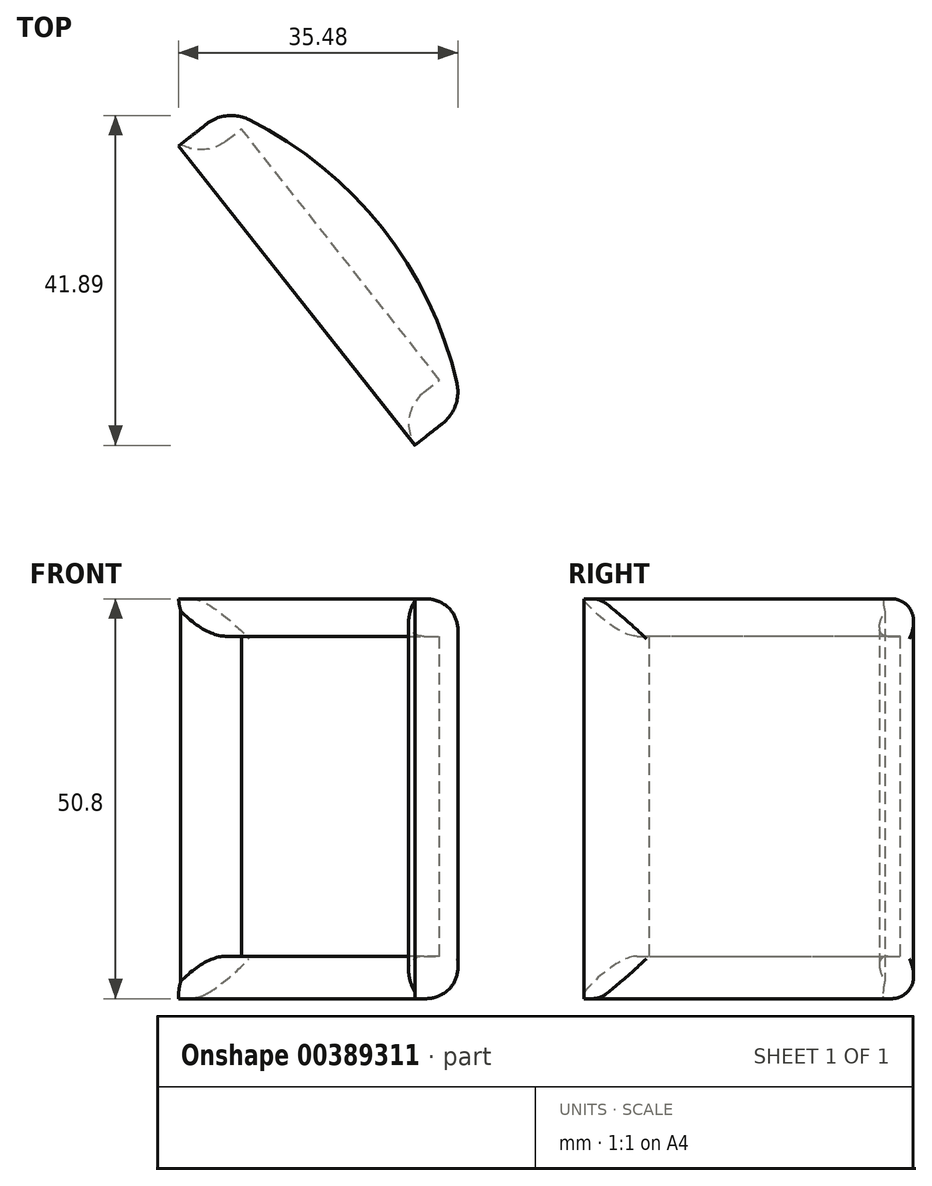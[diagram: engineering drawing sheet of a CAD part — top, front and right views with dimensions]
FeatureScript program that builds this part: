
annotation { "Feature Type Name" : "Feature", "Feature Type Description" : "" }
export const myFeature = defineFeature(function(context is Context, id is Id, definition is map)
    precondition{}
    {
        {
            var Q0;
            Q0=qCreatedBy(makeId("Top.planeOp"),FACE);
            var sketch = newSketch(context, id + "F0", { "sketchPlane" : qUnion([Q0])});
            skArc(sketch, "E0", {"start": v(30, 0) * mm, "mid": v(19.9, 22.87) * mm, "end": v(0, 38) * mm});
            skLineSegment(sketch, "E1", {"start": v(0, 38) * mm, "end": v(30, 0) * mm});
            skSolve(sketch);
        }
        {
            var Q0;
            Q0 = qSketchRegion(id + "F0", true);
            extrude(context, id + "F1", {"entities" : qUnion([Q0]), "depth" : 50.8 * mm});
        }
        {
            var Q0;
            Q0=makeQuery(id+"F1.opExtrude","SWEPT_FACE",FACE,{"disambiguationData":[OSD([sQuery(id+"F0.wireOp",EDGE,"E1")])]});
            var sketch = newSketch(context, id + "F2", { "sketchPlane" : qUnion([Q0])});
            skLineSegment(sketch, "E2", {"start": v(14.02, 5.4) * mm, "end": v(-26.62, 5.4) * mm});
            skLineSegment(sketch, "E3", {"start": v(14.02, 5.4) * mm, "end": v(14.02, 46.04) * mm});
            skLineSegment(sketch, "E4", {"start": v(-26.62, 5.4) * mm, "end": v(-26.62, 46.04) * mm});
            skLineSegment(sketch, "E5", {"start": v(-26.62, 46.04) * mm, "end": v(14.02, 46.04) * mm});
            skSolve(sketch);
        }
        {
            var Q0;
            Q0=makeQuery(id+"F2.imprint","IMPRINT",FACE,{"disambiguationData":[TD([[makeQuery(id+"F2.imprint","IMPRINT",EDGE,{"derivedFrom":sQuery(id+"F2.wireOp",EDGE,"E2")}),1.0]])]});
            extrude(context, id + "F3", {"entities" : qUnion([Q0]), "operationType" : NewBodyOperationType.ADD, "depth" : 7.62 * mm});
        }
        {
            var Q0;
            Q0=makeQuery(id+"F3.opExtrude","CAP_EDGE",EDGE,{"disambiguationData":[OSD([sQuery(id+"F2.wireOp",EDGE,"E5")])],"isStart":false});
            var Q1;
            Q1=makeQuery(id+"F3.opExtrude","CAP_EDGE",EDGE,{"disambiguationData":[OSD([sQuery(id+"F2.wireOp",EDGE,"E3")])],"isStart":false});
            var Q2;
            Q2=makeQuery(id+"F3.opExtrude","CAP_EDGE",EDGE,{"disambiguationData":[OSD([sQuery(id+"F2.wireOp",EDGE,"E4")])],"isStart":false});
            fillet(context, id + "F4", {"entities" : qUnion([Q0, Q1, Q2]), "radius" : 5.08 * mm, "tangentPropagation" : true, "allowEdgeOverflow" : false});
        }
        {
            var Q0;
            Q0=makeQuery(id+"F3.opExtrude","CAP_EDGE",EDGE,{"disambiguationData":[OSD([sQuery(id+"F2.wireOp",EDGE,"E2")])],"isStart":false});
            fillet(context, id + "F5", {"entities" : qUnion([Q0]), "radius" : 5.08 * mm, "tangentPropagation" : true, "allowEdgeOverflow" : false});
        }
        {
            var Q0;
            Q0=makeQuery(id+"F1.opExtrude","CAP_EDGE",EDGE,{"disambiguationData":[OSD([sQuery(id+"F0.wireOp",EDGE,"E0")])],"isStart":false});
            var Q1;
            {var subQ0=sQuery(id+"F0.wireOp",EDGE,"E1");var subQ1=sQuery(id+"F0.wireOp",EDGE,"E0");var subQ2=makeQuery(id+"F1.opExtrude","SWEPT_EDGE",EDGE,{"disambiguationData":[OSD([subQ1,subQ0]),TDD([makeQuery(id+"F0.imprint","INTERSECT",VERTEX,{"disambiguationData":[OD(0.0)],"derivedFrom":[subQ1,subQ0]})])]});Q1=makeQuery(id+"F3.boolean.opBoolean","MERGE",EDGE,{"derivedFrom":[subQ2,makeQuery(id+"F3.opExtrude","CAP_EDGE",EDGE,{"disambiguationData":[OSD([subQ1,subQ0]),TDD([makeQuery(id+"F2.imprint","IMPRINT",EDGE,{"derivedFrom":subQ2})])],"isStart":true})]});}
            var Q2;
            Q2=makeQuery(id+"F1.opExtrude","CAP_EDGE",EDGE,{"disambiguationData":[OSD([sQuery(id+"F0.wireOp",EDGE,"E0")])],"isStart":true});
            var Q3;
            {var subQ0=sQuery(id+"F0.wireOp",EDGE,"E1");var subQ1=sQuery(id+"F0.wireOp",EDGE,"E0");var subQ2=makeQuery(id+"F1.opExtrude","SWEPT_EDGE",EDGE,{"disambiguationData":[OSD([subQ1,subQ0]),TDD([makeQuery(id+"F0.imprint","INTERSECT",VERTEX,{"disambiguationData":[OD(1.0)],"derivedFrom":[subQ1,subQ0]})])]});Q3=makeQuery(id+"F3.boolean.opBoolean","MERGE",EDGE,{"derivedFrom":[subQ2,makeQuery(id+"F3.opExtrude","CAP_EDGE",EDGE,{"disambiguationData":[OSD([subQ1,subQ0]),TDD([makeQuery(id+"F2.imprint","IMPRINT",EDGE,{"derivedFrom":subQ2})])],"isStart":true})]});}
            fillet(context, id + "F6", {"entities" : qUnion([Q0, Q1, Q2, Q3]), "radius" : 5.08 * mm, "tangentPropagation" : true, "allowEdgeOverflow" : false});
        }
    });
